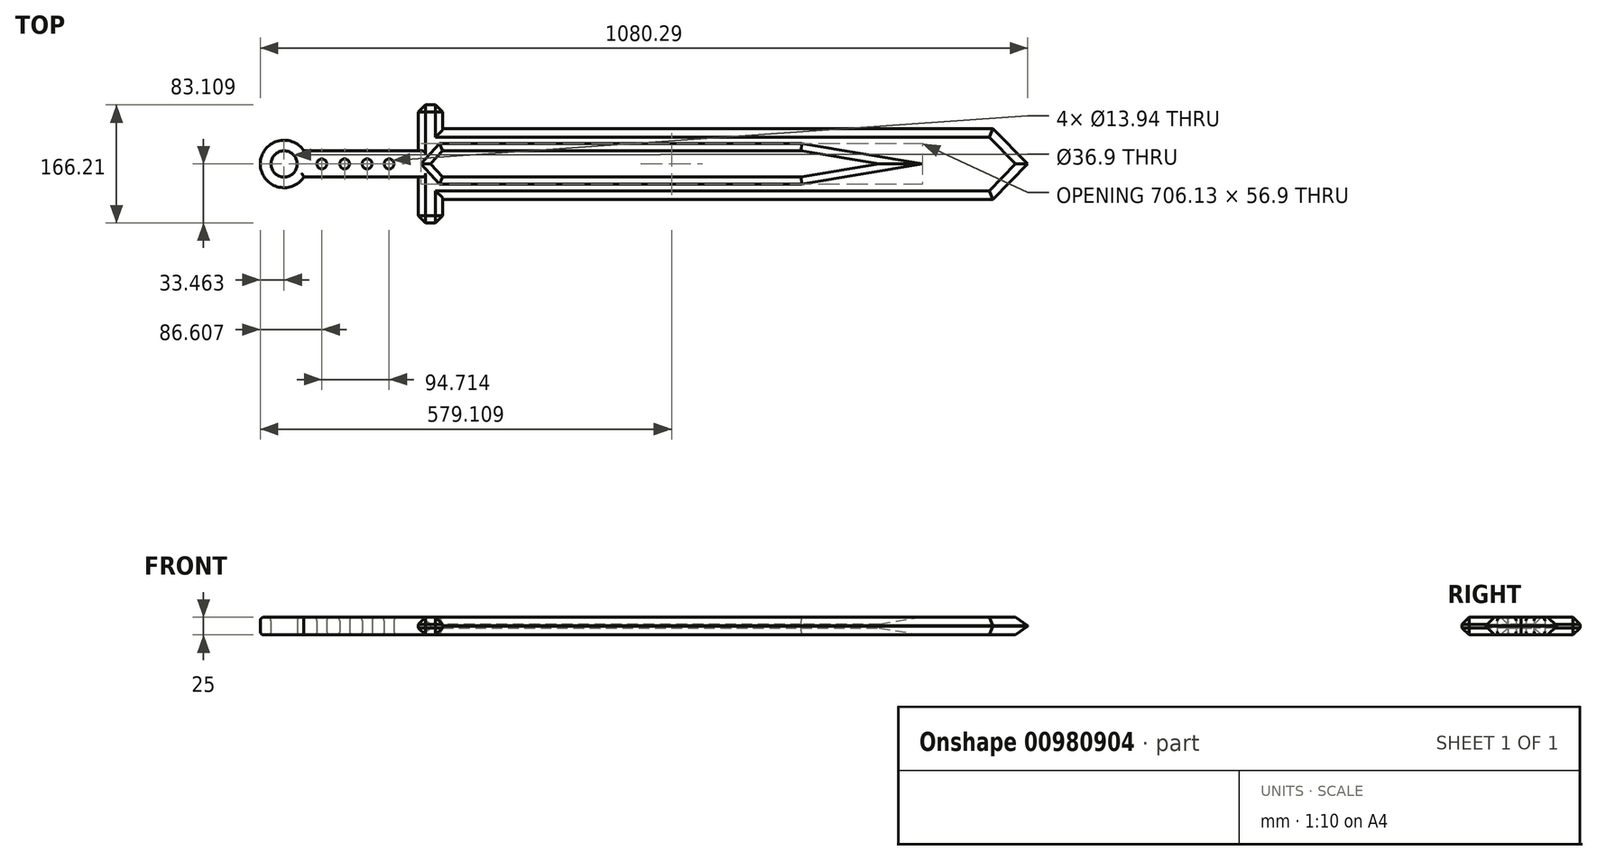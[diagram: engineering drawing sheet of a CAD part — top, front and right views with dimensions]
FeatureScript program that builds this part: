
annotation { "Feature Type Name" : "Feature", "Feature Type Description" : "" }
export const myFeature = defineFeature(function(context is Context, id is Id, definition is map)
    precondition{}
    {
        {
            var Q0;
            Q0=qCreatedBy(makeId("Top.planeOp"),FACE);
            var sketch = newSketch(context, id + "F0", { "sketchPlane" : qUnion([Q0])});
            skLineSegment(sketch, "E0.bottom", {"start": v(-98.52, 24.54) * mm, "end": v(-287.63, 24.54) * mm});
            skLineSegment(sketch, "E0.top", {"start": v(-98.52, -12.36) * mm, "end": v(-287.63, -12.36) * mm});
            skLineSegment(sketch, "E0.left", {"start": v(-98.52, 24.54) * mm, "end": v(-98.52, -12.36) * mm});
            skLineSegment(sketch, "E0.right", {"start": v(-287.63, 24.54) * mm, "end": v(-287.63, -12.36) * mm});
            skPoint(sketch, "E0.middle", {"position": v(-193.07, 6.09) * mm});
            skPoint(sketch, "E1", {"position": v(-287.63, 6.09) * mm});
            skCircle(sketch, "E2", {"center": v(-287.63, 6.09) * mm, "radius": 18.45 * mm});
            skCircle(sketch, "E3", {"center": v(-287.63, 6.09) * mm, "radius": 33.46 * mm});
            skLineSegment(sketch, "E4.bottom", {"start": v(-98.52, 89.2) * mm, "end": v(-64.29, 89.2) * mm});
            skLineSegment(sketch, "E4.top", {"start": v(-98.52, -77.02) * mm, "end": v(-64.29, -77.02) * mm});
            skLineSegment(sketch, "E4.left", {"start": v(-98.52, 89.2) * mm, "end": v(-98.52, -77.02) * mm});
            skPoint(sketch, "E4.middle", {"position": v(-81.4, 6.09) * mm});
            skPoint(sketch, "E4.cornerSnap0", {"position": v(-98.52, 6.09) * mm});
            skCircle(sketch, "E5", {"center": v(-234.48, 6.09) * mm, "radius": 6.97 * mm});
            skCircle(sketch, "E6", {"center": v(-202.4, 6.09) * mm, "radius": 6.97 * mm});
            skCircle(sketch, "E7", {"center": v(-170.7, 6.09) * mm, "radius": 6.97 * mm});
            skCircle(sketch, "E8", {"center": v(-139.77, 6.09) * mm, "radius": 6.97 * mm});
            skLineSegment(sketch, "E9", {"start": v(-98.52, 6.09) * mm, "end": v(759.2, 6.09) * mm});
            skLineSegment(sketch, "E10", {"start": v(-64.29, 55.95) * mm, "end": v(710, 55.95) * mm});
            skLineSegment(sketch, "E11", {"start": v(710, 55.95) * mm, "end": v(759.2, 6.09) * mm});
            skLineSegment(sketch, "E12.MirrorCS", {"start": v(-64.29, -43.77) * mm, "end": v(710, -43.77) * mm});
            skLineSegment(sketch, "E13.MirrorCS", {"start": v(710, -43.77) * mm, "end": v(759.2, 6.09) * mm});
            skLineSegment(sketch, "E14", {"start": v(-64.29, 24.54) * mm, "end": v(0, 24.54) * mm});
            skLineSegment(sketch, "E15.MirrorCS", {"start": v(-64.29, -12.36) * mm, "end": v(0, -12.36) * mm});
            skLineSegment(sketch, "E16", {"start": v(440.45, 24.54) * mm, "end": v(550.57, 6.09) * mm});
            skLineSegment(sketch, "E17.MirrorCS", {"start": v(440.45, -12.36) * mm, "end": v(550.57, 6.09) * mm});
            skLineSegment(sketch, "E18", {"start": v(0, 24.54) * mm, "end": v(220.23, 24.54) * mm});
            skLineSegment(sketch, "E19", {"start": v(220.23, 24.54) * mm, "end": v(440.45, 24.54) * mm});
            skLineSegment(sketch, "E20.MirrorCS", {"start": v(0, -12.36) * mm, "end": v(220.23, -12.36) * mm});
            skLineSegment(sketch, "E21.MirrorCS", {"start": v(220.23, -12.36) * mm, "end": v(440.45, -12.36) * mm});
            skLineSegment(sketch, "E22", {"start": v(0, 24.54) * mm, "end": v(0, -12.36) * mm});
            skLineSegment(sketch, "E23", {"start": v(-64.29, 24.54) * mm, "end": v(-81.4, 6.09) * mm});
            skLineSegment(sketch, "E24", {"start": v(-81.4, 6.09) * mm, "end": v(-64.29, -12.36) * mm});
            skLineSegment(sketch, "E25", {"start": v(-64.29, 89.2) * mm, "end": v(-64.29, 24.54) * mm});
            skLineSegment(sketch, "E26", {"start": v(-64.29, -12.36) * mm, "end": v(-64.29, -77.02) * mm});
            skSolve(sketch);
        }
        {
            var Q0;
            {var subQ0=sQuery(id+"F0.wireOp",EDGE,"E0.left");Q0=makeQuery(id+"F0.imprint","IMPRINT",FACE,{"disambiguationData":[TD([[makeQuery(id+"F0.imprint","IMPRINT",EDGE,{"derivedFrom":subQ0}),-1.0]])]});}
            var Q1;
            {var subQ2=sQuery(id+"F0.wireOp",EDGE,"E0.bottom");var subQ4=sQuery(id+"F0.wireOp",EDGE,"E3");var subQ5=makeQuery(id+"F0.imprint","INTERSECT",VERTEX,{"derivedFrom":[subQ2,subQ4]});Q1=makeQuery(id+"F0.imprint","IMPRINT",FACE,{"disambiguationData":[TD([[makeQuery(id+"F0.imprint","IMPRINT",EDGE,{"disambiguationData":[TD([[subQ5,-1.0]])],"derivedFrom":subQ4}),1.0]])]});}
            var Q2;
            {var subQ2=sQuery(id+"F0.wireOp",EDGE,"E0.bottom");var subQ4=sQuery(id+"F0.wireOp",EDGE,"E3");var subQ5=makeQuery(id+"F0.imprint","INTERSECT",VERTEX,{"derivedFrom":[subQ2,subQ4]});Q2=makeQuery(id+"F0.imprint","IMPRINT",FACE,{"disambiguationData":[TD([[makeQuery(id+"F0.imprint","IMPRINT",EDGE,{"disambiguationData":[TD([[subQ5,1.0]])],"derivedFrom":subQ4}),1.0]])]});}
            var Q3;
            {var subQ3=sQuery(id+"F0.wireOp",EDGE,"E4.bottom");Q3=makeQuery(id+"F0.imprint","IMPRINT",FACE,{"disambiguationData":[TD([[makeQuery(id+"F0.imprint","IMPRINT",EDGE,{"derivedFrom":subQ3}),-1.0]])]});}
            var Q4;
            {var subQ0=sQuery(id+"F0.wireOp",EDGE,"E4.left");var subQ1=sQuery(id+"F0.wireOp",EDGE,"E0.bottom");var subQ2=makeQuery(id+"F0.imprint","INTERSECT",VERTEX,{"derivedFrom":[subQ1,subQ0]});Q4=makeQuery(id+"F0.imprint","IMPRINT",FACE,{"disambiguationData":[TD([[makeQuery(id+"F0.imprint","IMPRINT",EDGE,{"disambiguationData":[TD([[subQ2,-1.0]])],"derivedFrom":subQ1}),1.0]])]});}
            var Q5;
            {var subQ0=sQuery(id+"F0.wireOp",EDGE,"E10");Q5=makeQuery(id+"F0.imprint","IMPRINT",FACE,{"disambiguationData":[TD([[makeQuery(id+"F0.imprint","IMPRINT",EDGE,{"derivedFrom":subQ0}),-1.0]])]});}
            var Q6;
            {var subQ0=sQuery(id+"F0.wireOp",EDGE,"E12.MirrorCS");Q6=makeQuery(id+"F0.imprint","IMPRINT",FACE,{"disambiguationData":[TD([[makeQuery(id+"F0.imprint","IMPRINT",EDGE,{"derivedFrom":subQ0}),1.0]])]});}
            var Q7;
            {var subQ6=sQuery(id+"F0.wireOp",EDGE,"E4.top");Q7=makeQuery(id+"F0.imprint","IMPRINT",FACE,{"disambiguationData":[TD([[makeQuery(id+"F0.imprint","IMPRINT",EDGE,{"derivedFrom":subQ6}),1.0]])]});}
            extrude(context, id + "F1", {"entities" : qUnion([Q0, Q1, Q2, Q3, Q4, Q5, Q6, Q7]), "depth" : 25 * mm, "offsetDistance" : 25 * mm});
        }
        {
            var Q0;
            Q0=makeQuery(id+"F1.opExtrude","CAP_EDGE",EDGE,{"disambiguationData":[OSD([sQuery(id+"F0.wireOp",EDGE,"E0.bottom")])],"isStart":false});
            var Q1;
            Q1=makeQuery(id+"F1.opExtrude","CAP_EDGE",EDGE,{"disambiguationData":[OSD([sQuery(id+"F0.wireOp",EDGE,"E0.top")])],"isStart":false});
            var Q2;
            Q2=makeQuery(id+"F1.opExtrude","CAP_EDGE",EDGE,{"disambiguationData":[OSD([sQuery(id+"F0.wireOp",EDGE,"E2")])],"isStart":false});
            var Q3;
            Q3=makeQuery(id+"F1.opExtrude","CAP_EDGE",EDGE,{"disambiguationData":[OSD([sQuery(id+"F0.wireOp",EDGE,"E3")])],"isStart":false});
            var Q4;
            Q4=makeQuery(id+"F1.opExtrude","CAP_EDGE",EDGE,{"disambiguationData":[OSD([sQuery(id+"F0.wireOp",EDGE,"E3")])],"isStart":true});
            var Q5;
            Q5=makeQuery(id+"F1.opExtrude","CAP_EDGE",EDGE,{"disambiguationData":[OSD([sQuery(id+"F0.wireOp",EDGE,"E2")])],"isStart":true});
            var Q6;
            Q6=makeQuery(id+"F1.opExtrude","CAP_EDGE",EDGE,{"disambiguationData":[OSD([sQuery(id+"F0.wireOp",EDGE,"E0.bottom")])],"isStart":true});
            var Q7;
            Q7=makeQuery(id+"F1.opExtrude","CAP_EDGE",EDGE,{"disambiguationData":[OSD([sQuery(id+"F0.wireOp",EDGE,"E0.top")])],"isStart":true});
            var Q8;
            Q8=makeQuery(id+"F1.opExtrude","CAP_EDGE",EDGE,{"disambiguationData":[OSD([sQuery(id+"F0.wireOp",EDGE,"E5")])],"isStart":true});
            var Q9;
            Q9=makeQuery(id+"F1.opExtrude","CAP_EDGE",EDGE,{"disambiguationData":[OSD([sQuery(id+"F0.wireOp",EDGE,"E6")])],"isStart":true});
            var Q10;
            Q10=makeQuery(id+"F1.opExtrude","CAP_EDGE",EDGE,{"disambiguationData":[OSD([sQuery(id+"F0.wireOp",EDGE,"E7")])],"isStart":true});
            var Q11;
            Q11=makeQuery(id+"F1.opExtrude","CAP_EDGE",EDGE,{"disambiguationData":[OSD([sQuery(id+"F0.wireOp",EDGE,"E8")])],"isStart":true});
            var Q12;
            Q12=makeQuery(id+"F1.opExtrude","CAP_EDGE",EDGE,{"disambiguationData":[OSD([sQuery(id+"F0.wireOp",EDGE,"E7")])],"isStart":false});
            var Q13;
            Q13=makeQuery(id+"F1.opExtrude","CAP_EDGE",EDGE,{"disambiguationData":[OSD([sQuery(id+"F0.wireOp",EDGE,"E8")])],"isStart":false});
            var Q14;
            Q14=makeQuery(id+"F1.opExtrude","CAP_EDGE",EDGE,{"disambiguationData":[OSD([sQuery(id+"F0.wireOp",EDGE,"E6")])],"isStart":false});
            var Q15;
            Q15=makeQuery(id+"F1.opExtrude","CAP_EDGE",EDGE,{"disambiguationData":[OSD([sQuery(id+"F0.wireOp",EDGE,"E5")])],"isStart":false});
            fillet(context, id + "F2", {"entities" : qUnion([Q0, Q1, Q2, Q3, Q4, Q5, Q6, Q7, Q8, Q9, Q10, Q11, Q12, Q13, Q14, Q15]), "radius" : 5 * mm, "tangentPropagation" : true, "allowEdgeOverflow" : false});
        }
        {
            var Q0;
            {var subQ0=sQuery(id+"F0.wireOp",EDGE,"E4.left");Q0=makeQuery(id+"F1.opExtrude","CAP_EDGE",EDGE,{"disambiguationData":[OSD([subQ0]),TDD([makeQuery(id+"F0.imprint","IMPRINT",EDGE,{"disambiguationData":[TD([[makeQuery(id+"F0.imprint","INTERSECT",VERTEX,{"derivedFrom":[sQuery(id+"F0.wireOp",EDGE,"E0.bottom"),subQ0]}),1.0]])],"derivedFrom":subQ0})])],"isStart":false});}
            var Q1;
            {var subQ0=sQuery(id+"F0.wireOp",EDGE,"E4.left");Q1=makeQuery(id+"F1.opExtrude","CAP_EDGE",EDGE,{"disambiguationData":[OSD([subQ0]),TDD([makeQuery(id+"F0.imprint","IMPRINT",EDGE,{"disambiguationData":[TD([[makeQuery(id+"F0.imprint","INTERSECT",VERTEX,{"derivedFrom":[sQuery(id+"F0.wireOp",EDGE,"E0.top"),subQ0]}),-1.0]])],"derivedFrom":subQ0})])],"isStart":false});}
            var Q2;
            {var subQ0=sQuery(id+"F0.wireOp",EDGE,"E4.left");Q2=makeQuery(id+"F1.opExtrude","CAP_EDGE",EDGE,{"disambiguationData":[OSD([subQ0]),TDD([makeQuery(id+"F0.imprint","IMPRINT",EDGE,{"disambiguationData":[TD([[makeQuery(id+"F0.imprint","INTERSECT",VERTEX,{"derivedFrom":[sQuery(id+"F0.wireOp",EDGE,"E0.bottom"),subQ0]}),1.0]])],"derivedFrom":subQ0})])],"isStart":true});}
            var Q3;
            {var subQ0=sQuery(id+"F0.wireOp",EDGE,"E4.left");Q3=makeQuery(id+"F1.opExtrude","CAP_EDGE",EDGE,{"disambiguationData":[OSD([subQ0]),TDD([makeQuery(id+"F0.imprint","IMPRINT",EDGE,{"disambiguationData":[TD([[makeQuery(id+"F0.imprint","INTERSECT",VERTEX,{"derivedFrom":[sQuery(id+"F0.wireOp",EDGE,"E0.top"),subQ0]}),-1.0]])],"derivedFrom":subQ0})])],"isStart":true});}
            var Q4;
            Q4=makeQuery(id+"F1.opExtrude","SWEPT_EDGE",EDGE,{"disambiguationData":[OSD([sQuery(id+"F0.wireOp",EDGE,"E4.top"),sQuery(id+"F0.wireOp",EDGE,"E4.right")])]});
            var Q5;
            Q5=makeQuery(id+"F1.opExtrude","CAP_EDGE",EDGE,{"disambiguationData":[OSD([sQuery(id+"F0.wireOp",EDGE,"E4.right")])],"isStart":false});
            var Q6;
            Q6=makeQuery(id+"F1.opExtrude","CAP_EDGE",EDGE,{"disambiguationData":[OSD([sQuery(id+"F0.wireOp",EDGE,"E4.right")])],"isStart":true});
            var Q7;
            Q7=makeQuery(id+"F1.opExtrude","CAP_EDGE",EDGE,{"disambiguationData":[OSD([sQuery(id+"F0.wireOp",EDGE,"E4.top")])],"isStart":true});
            var Q8;
            Q8=makeQuery(id+"F1.opExtrude","CAP_EDGE",EDGE,{"disambiguationData":[OSD([sQuery(id+"F0.wireOp",EDGE,"E4.bottom")])],"isStart":false});
            var Q9;
            Q9=makeQuery(id+"F1.opExtrude","CAP_EDGE",EDGE,{"disambiguationData":[OSD([sQuery(id+"F0.wireOp",EDGE,"E4.bottom")])],"isStart":true});
            var Q10;
            Q10=makeQuery(id+"F1.opExtrude","SWEPT_EDGE",EDGE,{"disambiguationData":[OSD([sQuery(id+"F0.wireOp",EDGE,"E4.bottom"),sQuery(id+"F0.wireOp",EDGE,"E4.right")])]});
            var Q11;
            Q11=makeQuery(id+"F1.opExtrude","SWEPT_EDGE",EDGE,{"disambiguationData":[OSD([sQuery(id+"F0.wireOp",EDGE,"E4.bottom"),sQuery(id+"F0.wireOp",EDGE,"E4.left")])]});
            var Q12;
            Q12=makeQuery(id+"F1.opExtrude","CAP_EDGE",EDGE,{"disambiguationData":[OSD([sQuery(id+"F0.wireOp",EDGE,"E4.top")])],"isStart":false});
            var Q13;
            Q13=makeQuery(id+"F1.opExtrude","SWEPT_EDGE",EDGE,{"disambiguationData":[OSD([sQuery(id+"F0.wireOp",EDGE,"E4.top"),sQuery(id+"F0.wireOp",EDGE,"E4.left")])]});
            var Q14;
            Q14=makeQuery(id+"F1.opExtrude","CAP_EDGE",EDGE,{"disambiguationData":[OSD([sQuery(id+"F0.wireOp",EDGE,"E15.MirrorCS"),sQuery(id+"F0.wireOp",EDGE,"E20.MirrorCS"),sQuery(id+"F0.wireOp",EDGE,"E21.MirrorCS")])],"isStart":false});
            var Q15;
            Q15=makeQuery(id+"F1.opExtrude","CAP_EDGE",EDGE,{"disambiguationData":[OSD([sQuery(id+"F0.wireOp",EDGE,"E14"),sQuery(id+"F0.wireOp",EDGE,"E18"),sQuery(id+"F0.wireOp",EDGE,"E19")])],"isStart":false});
            var Q16;
            Q16=makeQuery(id+"F1.opExtrude","CAP_EDGE",EDGE,{"disambiguationData":[OSD([sQuery(id+"F0.wireOp",EDGE,"E17.MirrorCS")])],"isStart":false});
            var Q17;
            Q17=makeQuery(id+"F1.opExtrude","CAP_EDGE",EDGE,{"disambiguationData":[OSD([sQuery(id+"F0.wireOp",EDGE,"E16")])],"isStart":false});
            var Q18;
            Q18=makeQuery(id+"F1.opExtrude","CAP_EDGE",EDGE,{"disambiguationData":[OSD([sQuery(id+"F0.wireOp",EDGE,"E17.MirrorCS")])],"isStart":true});
            var Q19;
            Q19=makeQuery(id+"F1.opExtrude","CAP_EDGE",EDGE,{"disambiguationData":[OSD([sQuery(id+"F0.wireOp",EDGE,"E15.MirrorCS"),sQuery(id+"F0.wireOp",EDGE,"E20.MirrorCS"),sQuery(id+"F0.wireOp",EDGE,"E21.MirrorCS")])],"isStart":true});
            var Q20;
            Q20=makeQuery(id+"F1.opExtrude","CAP_EDGE",EDGE,{"disambiguationData":[OSD([sQuery(id+"F0.wireOp",EDGE,"E14"),sQuery(id+"F0.wireOp",EDGE,"E18"),sQuery(id+"F0.wireOp",EDGE,"E19")])],"isStart":true});
            var Q21;
            Q21=makeQuery(id+"F1.opExtrude","CAP_EDGE",EDGE,{"disambiguationData":[OSD([sQuery(id+"F0.wireOp",EDGE,"E16")])],"isStart":true});
            var Q22;
            Q22=makeQuery(id+"F1.opExtrude","CAP_EDGE",EDGE,{"disambiguationData":[OSD([sQuery(id+"F0.wireOp",EDGE,"E24")])],"isStart":true});
            var Q23;
            Q23=makeQuery(id+"F1.opExtrude","CAP_EDGE",EDGE,{"disambiguationData":[OSD([sQuery(id+"F0.wireOp",EDGE,"E23")])],"isStart":true});
            var Q24;
            Q24=makeQuery(id+"F1.opExtrude","CAP_EDGE",EDGE,{"disambiguationData":[OSD([sQuery(id+"F0.wireOp",EDGE,"E23")])],"isStart":false});
            var Q25;
            Q25=makeQuery(id+"F1.opExtrude","CAP_EDGE",EDGE,{"disambiguationData":[OSD([sQuery(id+"F0.wireOp",EDGE,"E24")])],"isStart":false});
            var Q26;
            Q26=makeQuery(id+"F1.opExtrude","CAP_EDGE",EDGE,{"disambiguationData":[OSD([sQuery(id+"F0.wireOp",EDGE,"E25")])],"isStart":true});
            var Q27;
            Q27=makeQuery(id+"F1.opExtrude","CAP_EDGE",EDGE,{"disambiguationData":[OSD([sQuery(id+"F0.wireOp",EDGE,"E25")])],"isStart":false});
            var Q28;
            Q28=makeQuery(id+"F1.opExtrude","CAP_EDGE",EDGE,{"disambiguationData":[OSD([sQuery(id+"F0.wireOp",EDGE,"E26")])],"isStart":true});
            var Q29;
            Q29=makeQuery(id+"F1.opExtrude","CAP_EDGE",EDGE,{"disambiguationData":[OSD([sQuery(id+"F0.wireOp",EDGE,"E26")])],"isStart":false});
            chamfer(context, id + "F3", {"entities" : qUnion([Q0, Q1, Q2, Q3, Q4, Q5, Q6, Q7, Q8, Q9, Q10, Q11, Q12, Q13, Q14, Q15, Q16, Q17, Q18, Q19, Q20, Q21, Q22, Q23, Q24, Q25, Q26, Q27, Q28, Q29]), "width" : 10 * mm, "tangentPropagation" : true});
        }
        {
            var Q0;
            Q0=makeQuery(id+"F1.opExtrude","CAP_EDGE",EDGE,{"disambiguationData":[OSD([sQuery(id+"F0.wireOp",EDGE,"E12.MirrorCS")])],"isStart":false});
            var Q1;
            Q1=makeQuery(id+"F1.opExtrude","CAP_EDGE",EDGE,{"disambiguationData":[OSD([sQuery(id+"F0.wireOp",EDGE,"E12.MirrorCS")])],"isStart":true});
            var Q2;
            Q2=makeQuery(id+"F1.opExtrude","CAP_EDGE",EDGE,{"disambiguationData":[OSD([sQuery(id+"F0.wireOp",EDGE,"E13.MirrorCS")])],"isStart":false});
            var Q3;
            Q3=makeQuery(id+"F1.opExtrude","CAP_EDGE",EDGE,{"disambiguationData":[OSD([sQuery(id+"F0.wireOp",EDGE,"E13.MirrorCS")])],"isStart":true});
            var Q4;
            Q4=makeQuery(id+"F1.opExtrude","CAP_EDGE",EDGE,{"disambiguationData":[OSD([sQuery(id+"F0.wireOp",EDGE,"E10")])],"isStart":false});
            var Q5;
            Q5=makeQuery(id+"F1.opExtrude","CAP_EDGE",EDGE,{"disambiguationData":[OSD([sQuery(id+"F0.wireOp",EDGE,"E10")])],"isStart":true});
            var Q6;
            Q6=makeQuery(id+"F1.opExtrude","CAP_EDGE",EDGE,{"disambiguationData":[OSD([sQuery(id+"F0.wireOp",EDGE,"E11")])],"isStart":false});
            var Q7;
            Q7=makeQuery(id+"F1.opExtrude","CAP_EDGE",EDGE,{"disambiguationData":[OSD([sQuery(id+"F0.wireOp",EDGE,"E11")])],"isStart":true});
            chamfer(context, id + "F4", {"entities" : qUnion([Q0, Q1, Q2, Q3, Q4, Q5, Q6, Q7]), "width" : 12.15 * mm, "tangentPropagation" : true});
        }
    });
